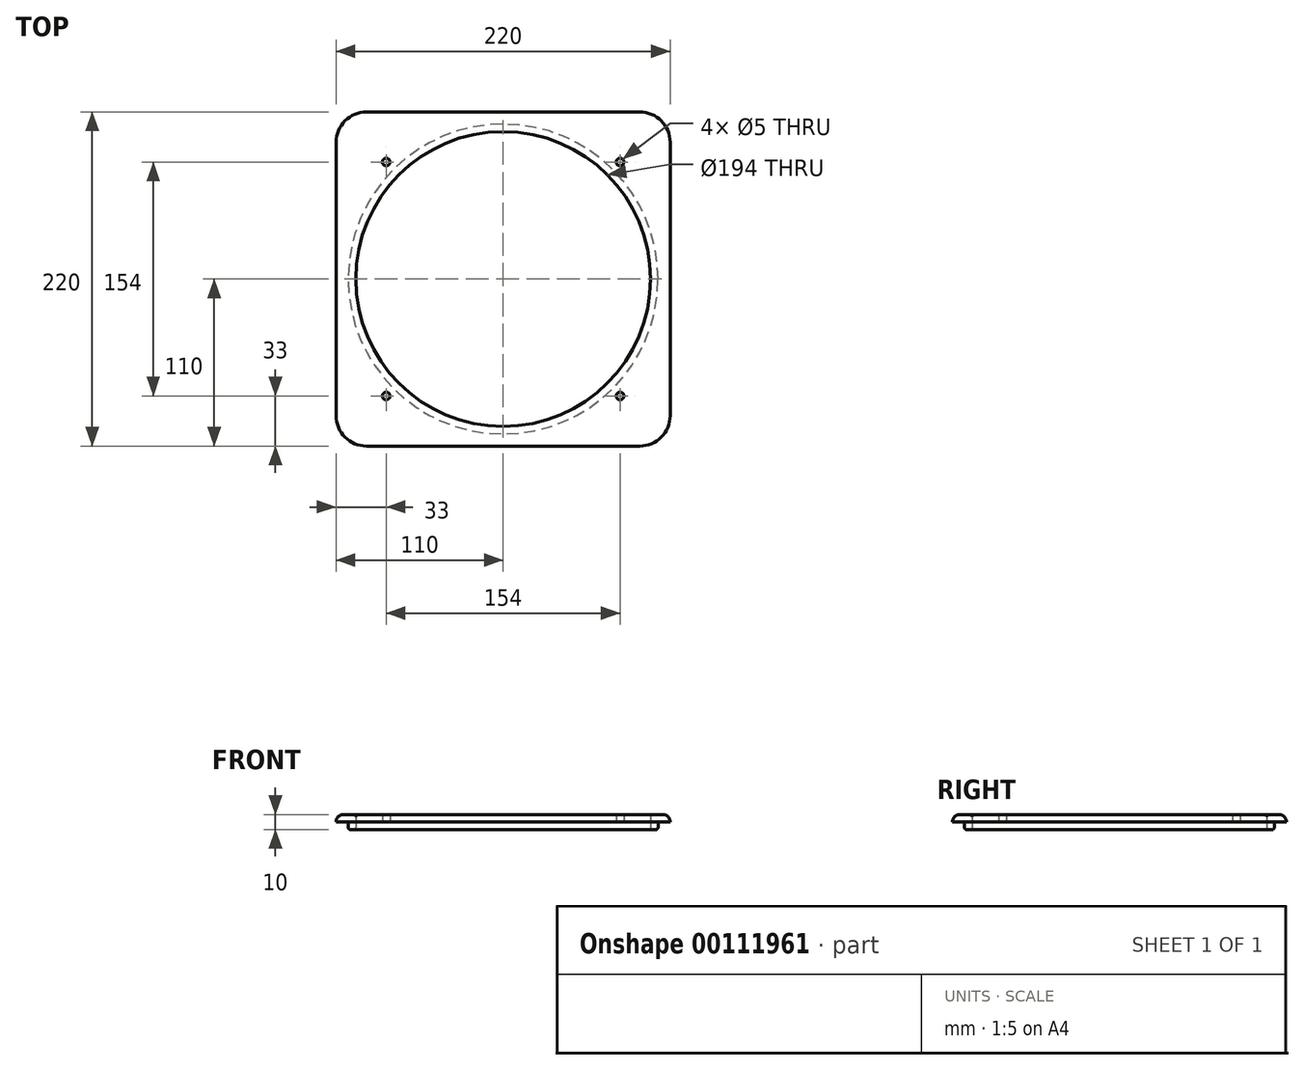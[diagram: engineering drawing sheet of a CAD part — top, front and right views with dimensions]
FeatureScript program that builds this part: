
annotation { "Feature Type Name" : "Feature", "Feature Type Description" : "" }
export const myFeature = defineFeature(function(context is Context, id is Id, definition is map)
    precondition{}
    {
        {
            var Q0;
            Q0=qCreatedBy(makeId("Top.planeOp"),FACE);
            var sketch = newSketch(context, id + "F0", { "sketchPlane" : qUnion([Q0])});
            skLineSegment(sketch, "E0.bottom", {"start": v(90, -110) * mm, "end": v(-90, -110) * mm});
            skLineSegment(sketch, "E0.top", {"start": v(90, 110) * mm, "end": v(-90, 110) * mm});
            skLineSegment(sketch, "E0.left", {"start": v(110, -90) * mm, "end": v(110, 90) * mm});
            skLineSegment(sketch, "E0.right", {"start": v(-110, -90) * mm, "end": v(-110, 90) * mm});
            skPoint(sketch, "E0.middle", {"position": v(0, 0) * mm});
            skCircle(sketch, "E1", {"center": v(0, 0) * mm, "radius": 97 * mm});
            skPoint(sketch, "E2.visualSharp", {"position": v(110, -110) * mm});
            skArc(sketch, "E2.filletArc", {"start": v(90, -110) * mm, "mid": v(104.14, -104.14) * mm, "end": v(110, -90) * mm});
            skPoint(sketch, "E3.visualSharp", {"position": v(-110, -110) * mm});
            skArc(sketch, "E3.filletArc", {"start": v(-110, -90) * mm, "mid": v(-104.14, -104.14) * mm, "end": v(-90, -110) * mm});
            skPoint(sketch, "E4.visualSharp", {"position": v(-110, 110) * mm});
            skArc(sketch, "E4.filletArc", {"start": v(-90, 110) * mm, "mid": v(-104.14, 104.14) * mm, "end": v(-110, 90) * mm});
            skPoint(sketch, "E5.visualSharp", {"position": v(110, 110) * mm});
            skArc(sketch, "E5.filletArc", {"start": v(110, 90) * mm, "mid": v(104.14, 104.14) * mm, "end": v(90, 110) * mm});
            skSolve(sketch);
        }
        {
            var Q0;
            Q0 = qSketchRegion(id + "F0", true);
            extrude(context, id + "F1", {"entities" : qUnion([Q0]), "depth" : 5 * mm});
        }
        {
            var Q0;
            Q0=makeQuery(id+"F1.opExtrude","CAP_FACE",FACE,{"disambiguationData":[OSD([sQuery(id+"F0.wireOp",EDGE,"E0.bottom"),sQuery(id+"F0.wireOp",EDGE,"E0.top"),sQuery(id+"F0.wireOp",EDGE,"E0.left"),sQuery(id+"F0.wireOp",EDGE,"E0.right"),sQuery(id+"F0.wireOp",EDGE,"E1")])],"isStart":true});
            var sketch = newSketch(context, id + "F2", { "sketchPlane" : qUnion([Q0])});
            skLineSegment(sketch, "E6", {"start": v(0, -110) * mm, "end": v(0, 110) * mm, "construction": true});
            skPoint(sketch, "E6.endSnap0", {"position": v(0, 110) * mm});
            skLineSegment(sketch, "E7", {"start": v(-110, 0) * mm, "end": v(110, 0) * mm, "construction": true});
            skPoint(sketch, "E8", {"position": v(0, 0) * mm});
            skCircle(sketch, "E9", {"center": v(-77, 77) * mm, "radius": 2.5 * mm});
            skCircle(sketch, "E10.1.0", {"center": v(-77, -77) * mm, "radius": 2.5 * mm});
            skCircle(sketch, "E10.2.0", {"center": v(77, -77) * mm, "radius": 2.5 * mm});
            skCircle(sketch, "E10.3.0", {"center": v(77, 77) * mm, "radius": 2.5 * mm});
            skSolve(sketch);
        }
        {
            var Q0;
            Q0=makeQuery(id+"F1.opExtrude","CAP_FACE",FACE,{"disambiguationData":[OSD([sQuery(id+"F0.wireOp",EDGE,"E0.bottom"),sQuery(id+"F0.wireOp",EDGE,"E0.top"),sQuery(id+"F0.wireOp",EDGE,"E0.left"),sQuery(id+"F0.wireOp",EDGE,"E0.right"),sQuery(id+"F0.wireOp",EDGE,"E1")])],"isStart":true});
            var sketch = newSketch(context, id + "F3", { "sketchPlane" : qUnion([Q0])});
            skCircle(sketch, "E11", {"center": v(0, 0) * mm, "radius": 97 * mm});
            skCircle(sketch, "E12", {"center": v(0, 0) * mm, "radius": 102 * mm});
            skSolve(sketch);
        }
        {
            var Q0;
            Q0 = qSketchRegion(id + "F3", true);
            extrude(context, id + "F4", {"entities" : qUnion([Q0]), "operationType" : NewBodyOperationType.ADD, "depth" : 5 * mm});
        }
        {
            var Q0;
            Q0=makeQuery(id+"F4.opExtrude","CAP_EDGE",EDGE,{"disambiguationData":[OSD([sQuery(id+"F3.wireOp",EDGE,"E11")])],"isStart":false});
            var Q1;
            Q1=makeQuery(id+"F4.opExtrude","CAP_EDGE",EDGE,{"disambiguationData":[OSD([sQuery(id+"F3.wireOp",EDGE,"E12")])],"isStart":false});
            var Q2;
            Q2=makeQuery(id+"F1.opExtrude","CAP_EDGE",EDGE,{"disambiguationData":[OSD([sQuery(id+"F0.wireOp",EDGE,"E1")])],"isStart":false});
            fillet(context, id + "F5", {"entities" : qUnion([Q0, Q1, Q2]), "radius" : 1.5 * mm, "tangentPropagation" : true, "allowEdgeOverflow" : false});
        }
        {
            var Q0;
            Q0=makeQuery(id+"F1.opExtrude","CAP_FACE",FACE,{"disambiguationData":[OSD([sQuery(id+"F0.wireOp",EDGE,"E0.bottom"),sQuery(id+"F0.wireOp",EDGE,"E0.top"),sQuery(id+"F0.wireOp",EDGE,"E0.left"),sQuery(id+"F0.wireOp",EDGE,"E0.right"),sQuery(id+"F0.wireOp",EDGE,"E1")])],"isStart":false});
            fillet(context, id + "F6", {"entities" : qUnion([Q0]), "radius" : 5 * mm, "tangentPropagation" : true, "allowEdgeOverflow" : false});
        }
        {
            var Q0;
            Q0=makeQuery(id+"F2.imprint","IMPRINT",FACE,{"disambiguationData":[TD([[makeQuery(id+"F2.imprint","IMPRINT",EDGE,{"derivedFrom":sQuery(id+"F2.wireOp",EDGE,"E9")}),1.0]])]});
            var Q1;
            Q1=makeQuery(id+"F2.imprint","IMPRINT",FACE,{"disambiguationData":[TD([[makeQuery(id+"F2.imprint","IMPRINT",EDGE,{"derivedFrom":sQuery(id+"F2.wireOp",EDGE,"E10.3.0")}),1.0]])]});
            var Q2;
            Q2=makeQuery(id+"F2.imprint","IMPRINT",FACE,{"disambiguationData":[TD([[makeQuery(id+"F2.imprint","IMPRINT",EDGE,{"derivedFrom":sQuery(id+"F2.wireOp",EDGE,"E10.2.0")}),1.0]])]});
            var Q3;
            Q3=makeQuery(id+"F2.imprint","IMPRINT",FACE,{"disambiguationData":[TD([[makeQuery(id+"F2.imprint","IMPRINT",EDGE,{"derivedFrom":sQuery(id+"F2.wireOp",EDGE,"E10.1.0")}),1.0]])]});
            var Q4;
            Q4=sQuery(id+"F2.wireOp",EDGE,"E9");
            var Q5;
            Q5=sQuery(id+"F2.wireOp",EDGE,"E10.1.0");
            var Q6;
            Q6=sQuery(id+"F2.wireOp",EDGE,"E10.3.0");
            var Q7;
            Q7=sQuery(id+"F2.wireOp",EDGE,"E10.2.0");
            extrude(context, id + "F7", {"entities" : qUnion([Q0, Q1, Q2, Q3]), "operationType" : NewBodyOperationType.REMOVE, "surfaceEntities" : qUnion([Q4, Q5, Q6, Q7]), "endBound" : BoundingType.UP_TO_NEXT, "oppositeDirection" : true, "depth" : 25 * mm});
        }
    });
